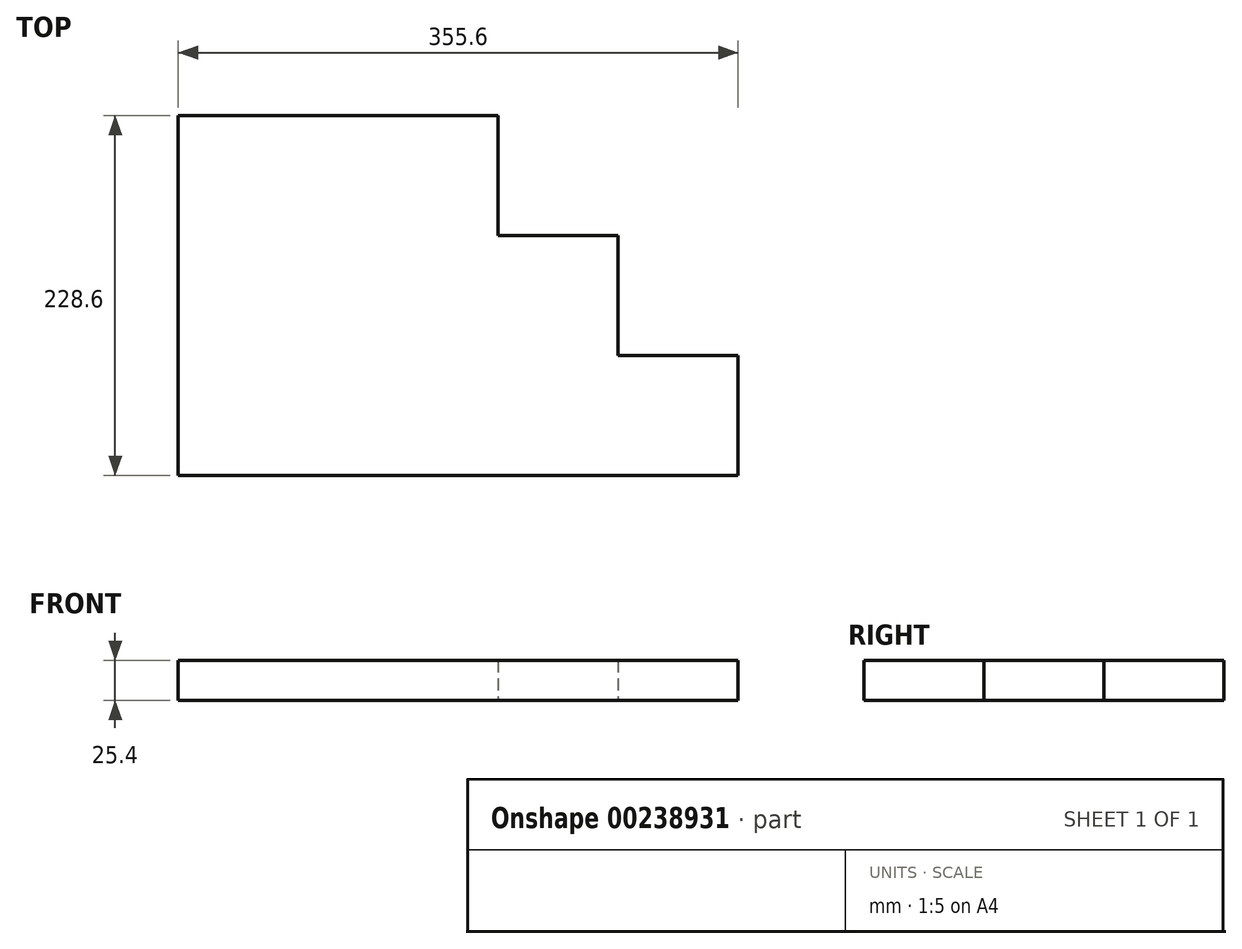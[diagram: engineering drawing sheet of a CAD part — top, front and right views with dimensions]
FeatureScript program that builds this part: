
annotation { "Feature Type Name" : "Feature", "Feature Type Description" : "" }
export const myFeature = defineFeature(function(context is Context, id is Id, definition is map)
    precondition{}
    {
        {
            var Q0;
            Q0=qCreatedBy(makeId("Top.planeOp"),FACE);
            var sketch = newSketch(context, id + "F0", { "sketchPlane" : qUnion([Q0])});
            skLineSegment(sketch, "E0", {"start": v(-120.57, -65.9) * mm, "end": v(235.03, -65.9) * mm});
            skLineSegment(sketch, "E1", {"start": v(235.03, -65.9) * mm, "end": v(235.03, 10.3) * mm});
            skLineSegment(sketch, "E2", {"start": v(235.03, 10.3) * mm, "end": v(158.83, 10.3) * mm});
            skLineSegment(sketch, "E3", {"start": v(158.83, 10.3) * mm, "end": v(158.83, 86.5) * mm});
            skLineSegment(sketch, "E4", {"start": v(158.83, 86.5) * mm, "end": v(82.63, 86.5) * mm});
            skLineSegment(sketch, "E5", {"start": v(82.63, 86.5) * mm, "end": v(82.63, 162.7) * mm});
            skLineSegment(sketch, "E6", {"start": v(82.63, 162.7) * mm, "end": v(-120.57, 162.7) * mm});
            skLineSegment(sketch, "E7", {"start": v(-120.57, 162.7) * mm, "end": v(-120.57, -65.9) * mm});
            skSolve(sketch);
        }
        {
            var Q0;
            Q0 = qSketchRegion(id + "F0", true);
            extrude(context, id + "F1", {"entities" : qUnion([Q0]), "depth" : 25.4 * mm});
        }
    });
